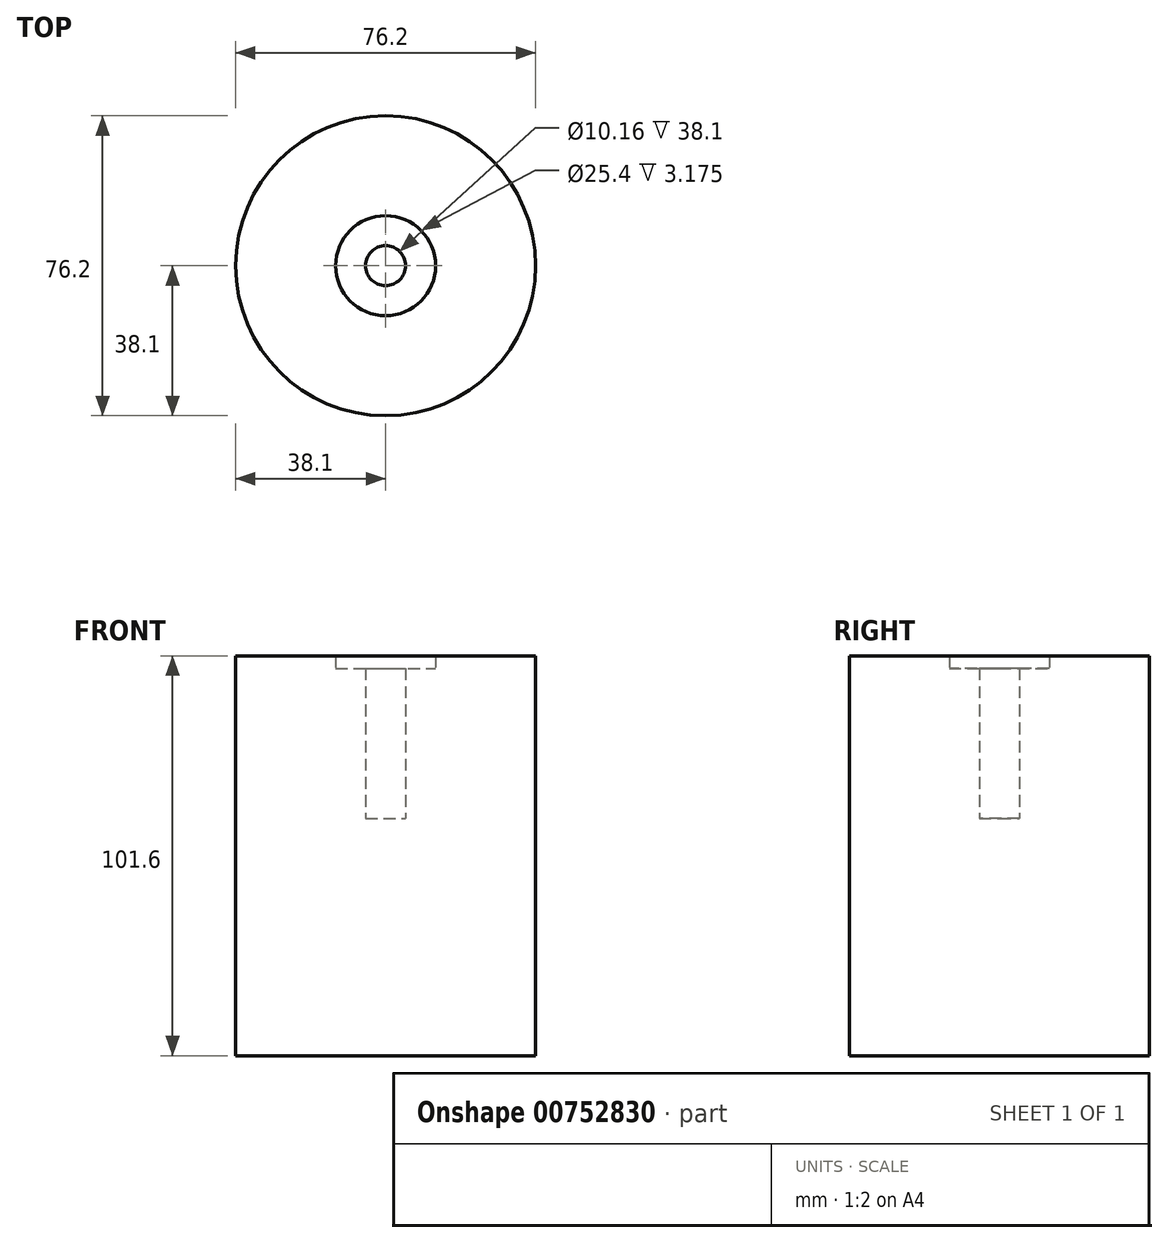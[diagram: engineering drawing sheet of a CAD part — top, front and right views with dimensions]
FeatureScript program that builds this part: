
annotation { "Feature Type Name" : "Feature", "Feature Type Description" : "" }
export const myFeature = defineFeature(function(context is Context, id is Id, definition is map)
    precondition{}
    {
        {
            var Q0;
            Q0=qCreatedBy(makeId("Right.planeOp"),FACE);
            var sketch = newSketch(context, id + "F0", { "sketchPlane" : qUnion([Q0])});
            skLineSegment(sketch, "E0.bottom", {"start": v(0, 0) * mm, "end": v(-38.1, 0) * mm});
            skLineSegment(sketch, "E0.top", {"start": v(-12.7, 101.6) * mm, "end": v(-38.1, 101.6) * mm});
            skLineSegment(sketch, "E0.left", {"start": v(0, 0) * mm, "end": v(0, 60.33) * mm});
            skLineSegment(sketch, "E0.right", {"start": v(-38.1, 0) * mm, "end": v(-38.1, 101.6) * mm});
            skLineSegment(sketch, "E1.top", {"start": v(0, 60.33) * mm, "end": v(-5.08, 60.33) * mm});
            skLineSegment(sketch, "E1.right", {"start": v(-5.08, 98.43) * mm, "end": v(-5.08, 60.33) * mm});
            skLineSegment(sketch, "E2.top", {"start": v(-5.08, 98.43) * mm, "end": v(-12.7, 98.43) * mm});
            skLineSegment(sketch, "E3", {"start": v(-12.7, 98.43) * mm, "end": v(-12.7, 101.6) * mm});
            skSolve(sketch);
        }
        {
            var Q0;
            Q0 = qSketchRegion(id + "F0", true);
            var Q1;
            Q1=sQuery(id+"F0.wireOp",EDGE,"E0.left");
            revolve(context, id + "F1", {"surfaceOperationType" : NewSurfaceOperationType.NEW, "entities" : qUnion([Q0]), "axis" : qUnion([Q1]), "revolveType" : RevolveType.FULL});
        }
    });
